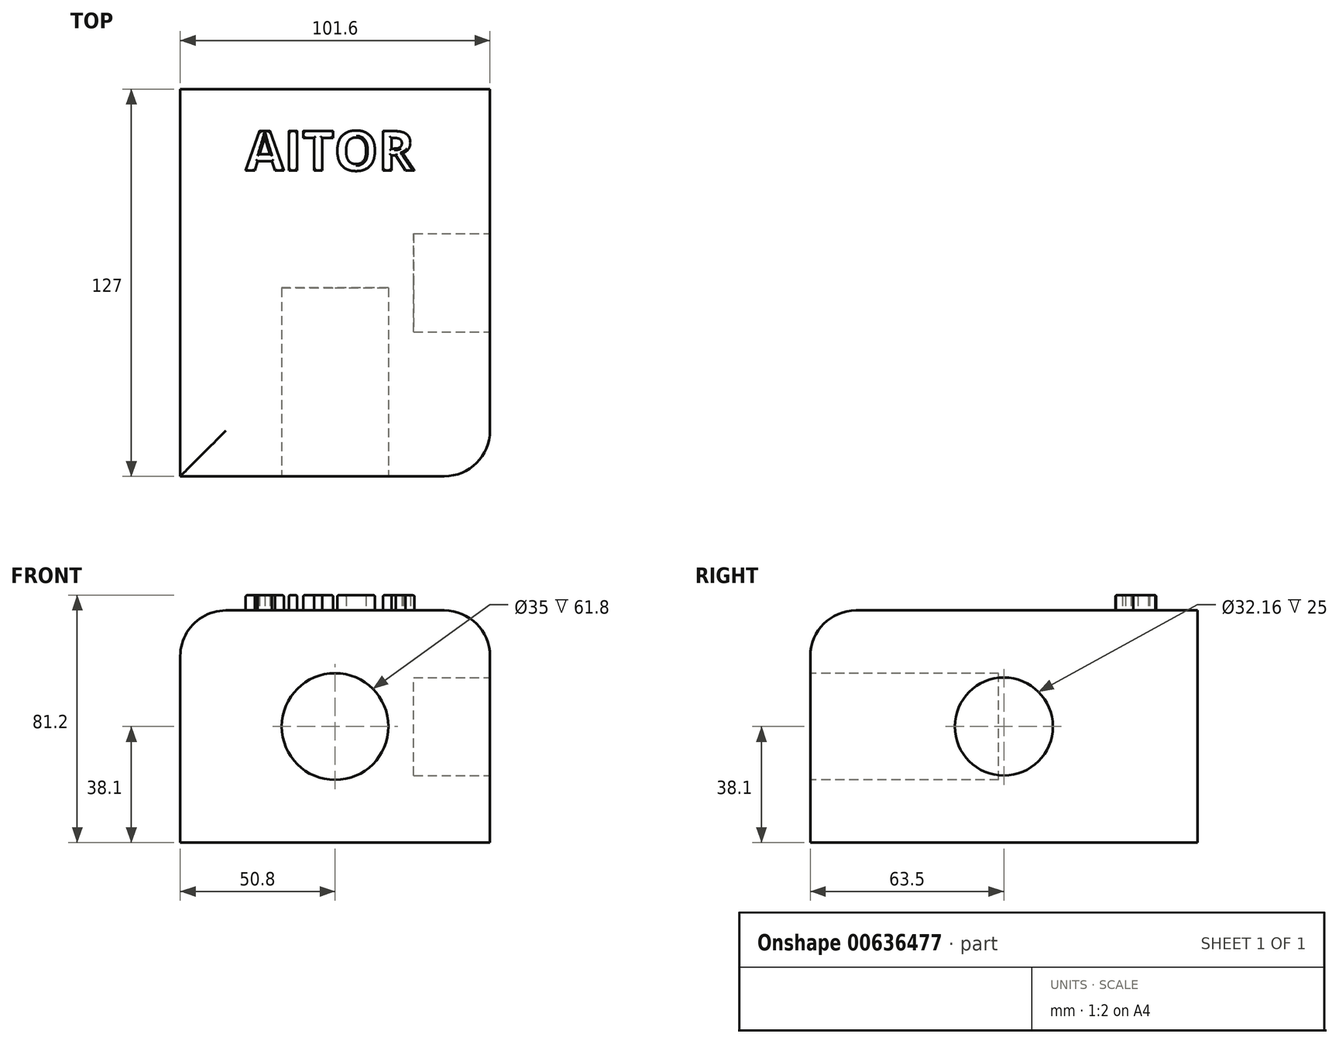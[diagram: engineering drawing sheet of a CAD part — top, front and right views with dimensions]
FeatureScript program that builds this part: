
annotation { "Feature Type Name" : "Feature", "Feature Type Description" : "" }
export const myFeature = defineFeature(function(context is Context, id is Id, definition is map)
    precondition{}
    {
        {
            var Q0;
            Q0=qCreatedBy(makeId("Front.planeOp"),FACE);
            var sketch = newSketch(context, id + "F0", { "sketchPlane" : qUnion([Q0])});
            skLineSegment(sketch, "E0.bottom", {"start": v(-50.8, 38.1) * mm, "end": v(50.8, 38.1) * mm});
            skLineSegment(sketch, "E0.top", {"start": v(-50.8, -38.1) * mm, "end": v(50.8, -38.1) * mm});
            skLineSegment(sketch, "E0.left", {"start": v(-50.8, 38.1) * mm, "end": v(-50.8, -38.1) * mm});
            skLineSegment(sketch, "E0.right", {"start": v(50.8, 38.1) * mm, "end": v(50.8, -38.1) * mm});
            skLineSegment(sketch, "E1", {"start": v(-50.8, 38.1) * mm, "end": v(50.8, -38.1) * mm});
            skSolve(sketch);
        }
        {
            var Q0;
            Q0 = qSketchRegion(id + "F0", true);
            extrude(context, id + "F1", {"entities" : qUnion([Q0]), "endBound" : BoundingType.SYMMETRIC, "depth" : 127 * mm, "offsetDistance" : 25.4 * mm});
        }
        {
            var Q0;
            Q0=makeQuery(id+"F1.opExtrude","CAP_FACE",FACE,{"disambiguationData":[OSD([sQuery(id+"F0.wireOp",EDGE,"E0.bottom"),sQuery(id+"F0.wireOp",EDGE,"E0.top"),sQuery(id+"F0.wireOp",EDGE,"E0.left"),sQuery(id+"F0.wireOp",EDGE,"E0.right")])],"isStart":false});
            var sketch = newSketch(context, id + "F2", { "sketchPlane" : qUnion([Q0])});
            skCircle(sketch, "E2", {"center": v(0, 0) * mm, "radius": 17.5 * mm});
            skSolve(sketch);
        }
        {
            var Q0;
            Q0 = qSketchRegion(id + "F2", true);
            extrude(context, id + "F3", {"entities" : qUnion([Q0]), "operationType" : NewBodyOperationType.REMOVE, "oppositeDirection" : true, "depth" : 61.8 * mm, "offsetDistance" : 25 * mm});
        }
        {
            var Q0;
            Q0=makeQuery(id+"F1.opExtrude","CAP_EDGE",EDGE,{"disambiguationData":[OSD([sQuery(id+"F0.wireOp",EDGE,"E0.bottom")])],"isStart":false});
            var Q1;
            Q1=makeQuery(id+"F1.opExtrude","SWEPT_EDGE",EDGE,{"disambiguationData":[OSD([sQuery(id+"F0.wireOp",EDGE,"E0.bottom"),sQuery(id+"F0.wireOp",EDGE,"E0.right")])]});
            var Q2;
            Q2=makeQuery(id+"F1.opExtrude","SWEPT_EDGE",EDGE,{"disambiguationData":[OSD([sQuery(id+"F0.wireOp",EDGE,"E0.bottom"),sQuery(id+"F0.wireOp",EDGE,"E0.left"),sQuery(id+"F0.wireOp",EDGE,"E1")])]});
            var Q3;
            Q3=makeQuery(id+"F1.opExtrude","CAP_EDGE",EDGE,{"disambiguationData":[OSD([sQuery(id+"F0.wireOp",EDGE,"E0.right")])],"isStart":false});
            fillet(context, id + "F4", {"entities" : qUnion([Q0, Q1, Q2, Q3]), "radius" : 15 * mm, "tangentPropagation" : true, "allowEdgeOverflow" : false});
        }
        {
            var Q0;
            Q0=makeQuery(id+"F1.opExtrude","SWEPT_FACE",FACE,{"disambiguationData":[OSD([sQuery(id+"F0.wireOp",EDGE,"E0.bottom")])]});
            var sketch = newSketch(context, id + "F5", { "sketchPlane" : qUnion([Q0])});
            skText(sketch, "E3", { "text": "AITOR\n", "fontName": "OpenSans-Bold.ttf"});
            const initialGuessF5  = {"E3": [-0.02932, 0.0368, 1, 0, 0.01305]};
            skSetInitialGuess(sketch, initialGuessF5);
            skSolve(sketch);
        }
        {
            var Q0;
            Q0 = qSketchRegion(id + "F5", true);
            extrude(context, id + "F6", {"entities" : qUnion([Q0]), "operationType" : NewBodyOperationType.ADD, "depth" : 5 * mm, "offsetDistance" : 25 * mm});
        }
        {
            var Q0;
            Q0=makeQuery(id+"F6.opExtrude","CAP_FACE",FACE,{"disambiguationData":[OSD([sQuery(id+"F5.wireOp",EDGE,"E3.sketch_text.stroke-0"),sQuery(id+"F5.wireOp",EDGE,"E3.sketch_text.stroke-1"),sQuery(id+"F5.wireOp",EDGE,"E3.sketch_text.stroke-2"),sQuery(id+"F5.wireOp",EDGE,"E3.sketch_text.stroke-3"),sQuery(id+"F5.wireOp",EDGE,"E3.sketch_text.stroke-4"),sQuery(id+"F5.wireOp",EDGE,"E3.sketch_text.stroke-5"),sQuery(id+"F5.wireOp",EDGE,"E3.sketch_text.stroke-6"),sQuery(id+"F5.wireOp",EDGE,"E3.sketch_text.stroke-7"),sQuery(id+"F5.wireOp",EDGE,"E3.sketch_text.stroke-8"),sQuery(id+"F5.wireOp",EDGE,"E3.sketch_text.stroke-9"),sQuery(id+"F5.wireOp",EDGE,"E3.sketch_text.stroke-10"),sQuery(id+"F5.wireOp",EDGE,"E3.sketch_text.stroke-11")])],"isStart":false});
            var Q1;
            Q1=makeQuery(id+"F6.opExtrude","CAP_FACE",FACE,{"disambiguationData":[OSD([sQuery(id+"F5.wireOp",EDGE,"E3.sketch_text.stroke-12"),sQuery(id+"F5.wireOp",EDGE,"E3.sketch_text.stroke-13"),sQuery(id+"F5.wireOp",EDGE,"E3.sketch_text.stroke-14"),sQuery(id+"F5.wireOp",EDGE,"E3.sketch_text.stroke-15")])],"isStart":false});
            var Q2;
            Q2=makeQuery(id+"F6.opExtrude","CAP_FACE",FACE,{"disambiguationData":[OSD([sQuery(id+"F5.wireOp",EDGE,"E3.sketch_text.stroke-16"),sQuery(id+"F5.wireOp",EDGE,"E3.sketch_text.stroke-17"),sQuery(id+"F5.wireOp",EDGE,"E3.sketch_text.stroke-18"),sQuery(id+"F5.wireOp",EDGE,"E3.sketch_text.stroke-19"),sQuery(id+"F5.wireOp",EDGE,"E3.sketch_text.stroke-20"),sQuery(id+"F5.wireOp",EDGE,"E3.sketch_text.stroke-21"),sQuery(id+"F5.wireOp",EDGE,"E3.sketch_text.stroke-22"),sQuery(id+"F5.wireOp",EDGE,"E3.sketch_text.stroke-23")])],"isStart":false});
            var Q3;
            Q3=makeQuery(id+"F6.opExtrude","CAP_FACE",FACE,{"disambiguationData":[OSD([sQuery(id+"F5.wireOp",EDGE,"E3.sketch_text.stroke-24"),sQuery(id+"F5.wireOp",EDGE,"E3.sketch_text.stroke-25"),sQuery(id+"F5.wireOp",EDGE,"E3.sketch_text.stroke-26"),sQuery(id+"F5.wireOp",EDGE,"E3.sketch_text.stroke-27"),sQuery(id+"F5.wireOp",EDGE,"E3.sketch_text.stroke-28"),sQuery(id+"F5.wireOp",EDGE,"E3.sketch_text.stroke-29"),sQuery(id+"F5.wireOp",EDGE,"E3.sketch_text.stroke-30"),sQuery(id+"F5.wireOp",EDGE,"E3.sketch_text.stroke-31"),sQuery(id+"F5.wireOp",EDGE,"E3.sketch_text.stroke-32"),sQuery(id+"F5.wireOp",EDGE,"E3.sketch_text.stroke-33"),sQuery(id+"F5.wireOp",EDGE,"E3.sketch_text.stroke-34"),sQuery(id+"F5.wireOp",EDGE,"E3.sketch_text.stroke-35"),sQuery(id+"F5.wireOp",EDGE,"E3.sketch_text.stroke-36"),sQuery(id+"F5.wireOp",EDGE,"E3.sketch_text.stroke-37")])],"isStart":false});
            var Q4;
            Q4=makeQuery(id+"F6.opExtrude","CAP_FACE",FACE,{"disambiguationData":[OSD([sQuery(id+"F5.wireOp",EDGE,"E3.sketch_text.stroke-38"),sQuery(id+"F5.wireOp",EDGE,"E3.sketch_text.stroke-39"),sQuery(id+"F5.wireOp",EDGE,"E3.sketch_text.stroke-40"),sQuery(id+"F5.wireOp",EDGE,"E3.sketch_text.stroke-41"),sQuery(id+"F5.wireOp",EDGE,"E3.sketch_text.stroke-42"),sQuery(id+"F5.wireOp",EDGE,"E3.sketch_text.stroke-43"),sQuery(id+"F5.wireOp",EDGE,"E3.sketch_text.stroke-44"),sQuery(id+"F5.wireOp",EDGE,"E3.sketch_text.stroke-45"),sQuery(id+"F5.wireOp",EDGE,"E3.sketch_text.stroke-46"),sQuery(id+"F5.wireOp",EDGE,"E3.sketch_text.stroke-47"),sQuery(id+"F5.wireOp",EDGE,"E3.sketch_text.stroke-48"),sQuery(id+"F5.wireOp",EDGE,"E3.sketch_text.stroke-49"),sQuery(id+"F5.wireOp",EDGE,"E3.sketch_text.stroke-50"),sQuery(id+"F5.wireOp",EDGE,"E3.sketch_text.stroke-51"),sQuery(id+"F5.wireOp",EDGE,"E3.sketch_text.stroke-52"),sQuery(id+"F5.wireOp",EDGE,"E3.sketch_text.stroke-53"),sQuery(id+"F5.wireOp",EDGE,"E3.sketch_text.stroke-54"),sQuery(id+"F5.wireOp",EDGE,"E3.sketch_text.stroke-55"),sQuery(id+"F5.wireOp",EDGE,"E3.sketch_text.stroke-56")])],"isStart":false});
            fillet(context, id + "F7", {"entities" : qUnion([Q0, Q1, Q2, Q3, Q4]), "radius" : 0.5 * mm, "tangentPropagation" : true, "allowEdgeOverflow" : false});
        }
        {
            var Q0;
            Q0=makeQuery(id+"F1.opExtrude","SWEPT_FACE",FACE,{"disambiguationData":[OSD([sQuery(id+"F0.wireOp",EDGE,"E0.right")])]});
            var sketch = newSketch(context, id + "F8", { "sketchPlane" : qUnion([Q0])});
            skCircle(sketch, "E4", {"center": v(0, 0) * mm, "radius": 16.08 * mm});
            skSolve(sketch);
        }
        {
            var Q0;
            Q0 = qSketchRegion(id + "F8", true);
            extrude(context, id + "F9", {"entities" : qUnion([Q0]), "operationType" : NewBodyOperationType.REMOVE, "oppositeDirection" : true, "depth" : 25 * mm, "offsetDistance" : 25 * mm});
        }
    });
